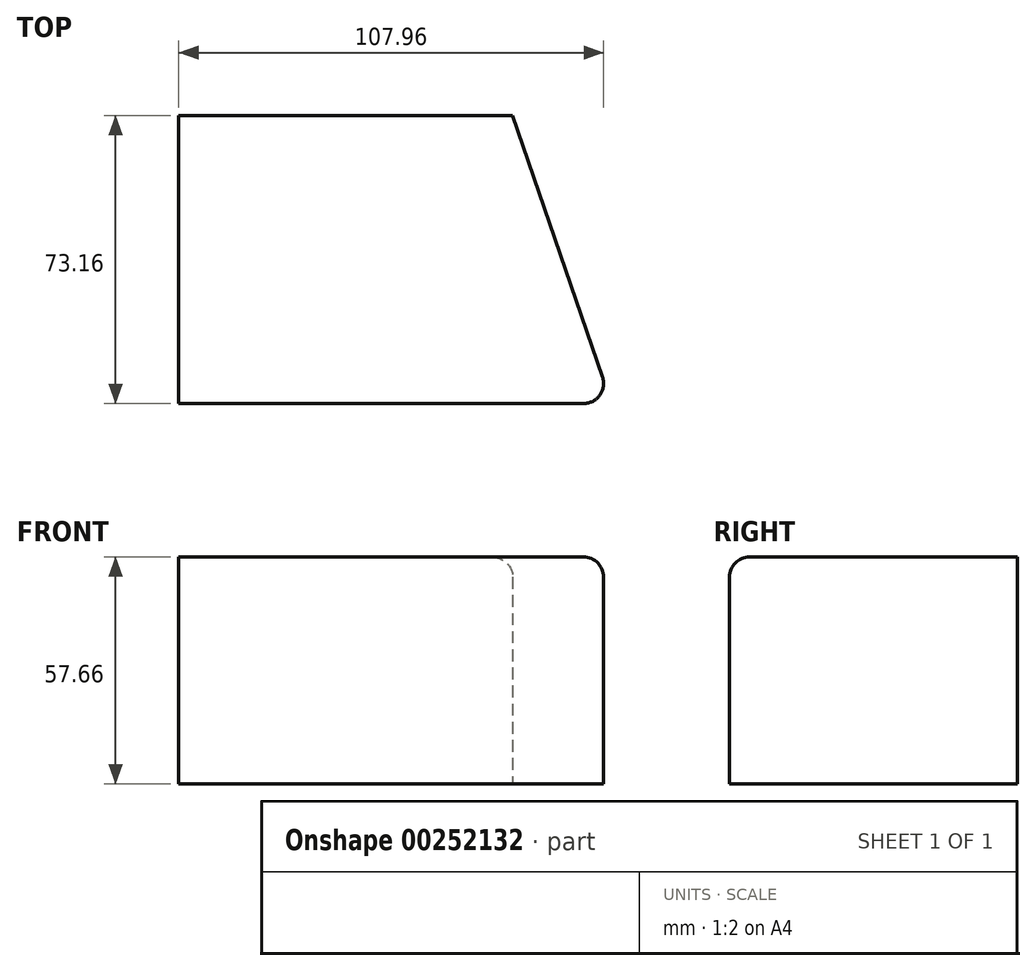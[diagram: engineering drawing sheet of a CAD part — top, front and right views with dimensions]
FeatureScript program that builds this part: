
annotation { "Feature Type Name" : "Feature", "Feature Type Description" : "" }
export const myFeature = defineFeature(function(context is Context, id is Id, definition is map)
    precondition{}
    {
        {
            var Q0;
            Q0=qCreatedBy(makeId("Top.planeOp"),FACE);
            var sketch = newSketch(context, id + "F0", { "sketchPlane" : qUnion([Q0])});
            skLineSegment(sketch, "E0", {"start": v(0, 0) * mm, "end": v(-110, 0) * mm});
            skLineSegment(sketch, "E1", {"start": v(-110, 0) * mm, "end": v(-110, 73.16) * mm});
            skLineSegment(sketch, "E2", {"start": v(-110, 73.16) * mm, "end": v(-25.13, 73.16) * mm});
            skLineSegment(sketch, "E3", {"start": v(-25.13, 73.16) * mm, "end": v(0, 0) * mm});
            skSolve(sketch);
        }
        {
            var Q0;
            Q0=makeQuery(id+"F0.imprint","IMPRINT",FACE,{"disambiguationData":[TD([[makeQuery(id+"F0.imprint","IMPRINT",EDGE,{"derivedFrom":sQuery(id+"F0.wireOp",EDGE,"E0")}),-1.0]])]});
            extrude(context, id + "F1", {"entities" : qUnion([Q0]), "depth" : 57.66 * mm});
        }
        {
            var Q0;
            Q0=makeQuery(id+"F1.opExtrude","CAP_EDGE",EDGE,{"disambiguationData":[OSD([sQuery(id+"F0.wireOp",EDGE,"E0")])],"isStart":false});
            var Q1;
            Q1=makeQuery(id+"F1.opExtrude","CAP_EDGE",EDGE,{"disambiguationData":[OSD([sQuery(id+"F0.wireOp",EDGE,"E3")])],"isStart":false});
            var Q2;
            Q2=makeQuery(id+"F1.opExtrude","SWEPT_EDGE",EDGE,{"disambiguationData":[OSD([sQuery(id+"F0.wireOp",EDGE,"E0"),sQuery(id+"F0.wireOp",EDGE,"E3")])]});
            fillet(context, id + "F2", {"entities" : qUnion([Q0, Q1, Q2]), "radius" : 5.08 * mm, "tangentPropagation" : true, "allowEdgeOverflow" : false});
        }
    });
